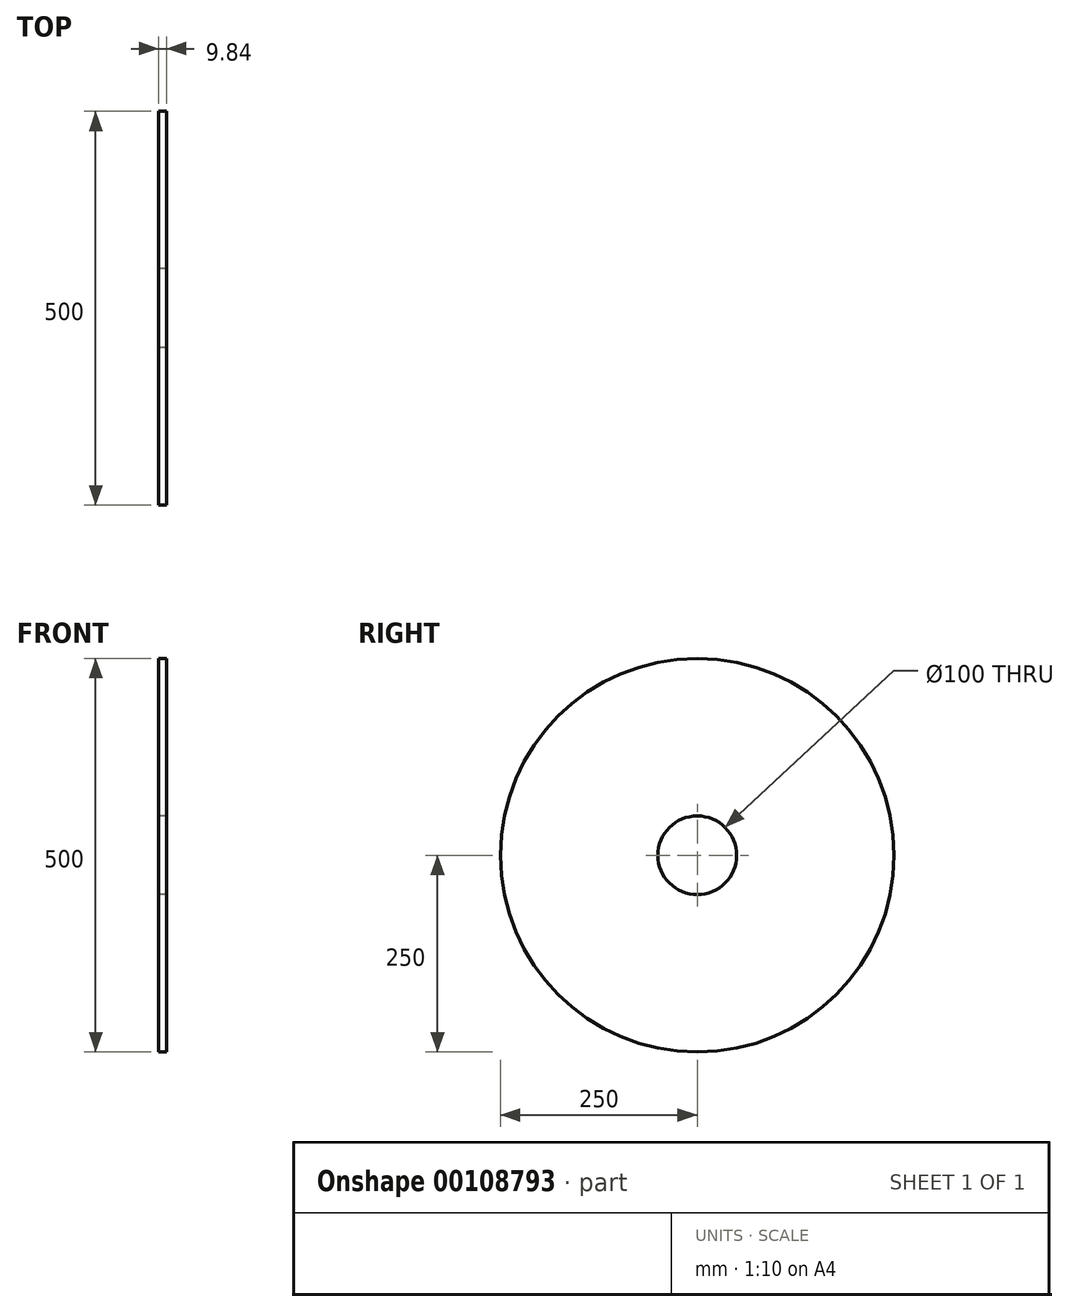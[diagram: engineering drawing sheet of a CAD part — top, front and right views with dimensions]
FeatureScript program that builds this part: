
annotation { "Feature Type Name" : "Feature", "Feature Type Description" : "" }
export const myFeature = defineFeature(function(context is Context, id is Id, definition is map)
    precondition{}
    {
        {
            var Q0;
            Q0=qCreatedBy(makeId("Front.planeOp"),FACE);
            var sketch = newSketch(context, id + "F0", { "sketchPlane" : qUnion([Q0])});
            skLineSegment(sketch, "E0", {"start": v(0, 0) * mm, "end": v(0, 250) * mm});
            skLineSegment(sketch, "E1", {"start": v(0, 250) * mm, "end": v(9.84, 250) * mm});
            skLineSegment(sketch, "E2", {"start": v(9.84, 250) * mm, "end": v(9.84, 50) * mm});
            skLineSegment(sketch, "E3", {"start": v(9.84, 50) * mm, "end": v(0, 50) * mm});
            skLineSegment(sketch, "E4", {"start": v(-184.23, 0) * mm, "end": v(318.21, 0) * mm, "construction": true});
            skSolve(sketch);
        }
        {
            var Q0;
            Q0 = qSketchRegion(id + "F0", true);
            var Q1;
            Q1=sQuery(id+"F0.wireOp",EDGE,"E4");
            revolve(context, id + "F1", {"entities" : qUnion([Q0]), "axis" : qUnion([Q1]), "revolveType" : RevolveType.FULL});
        }
    });
